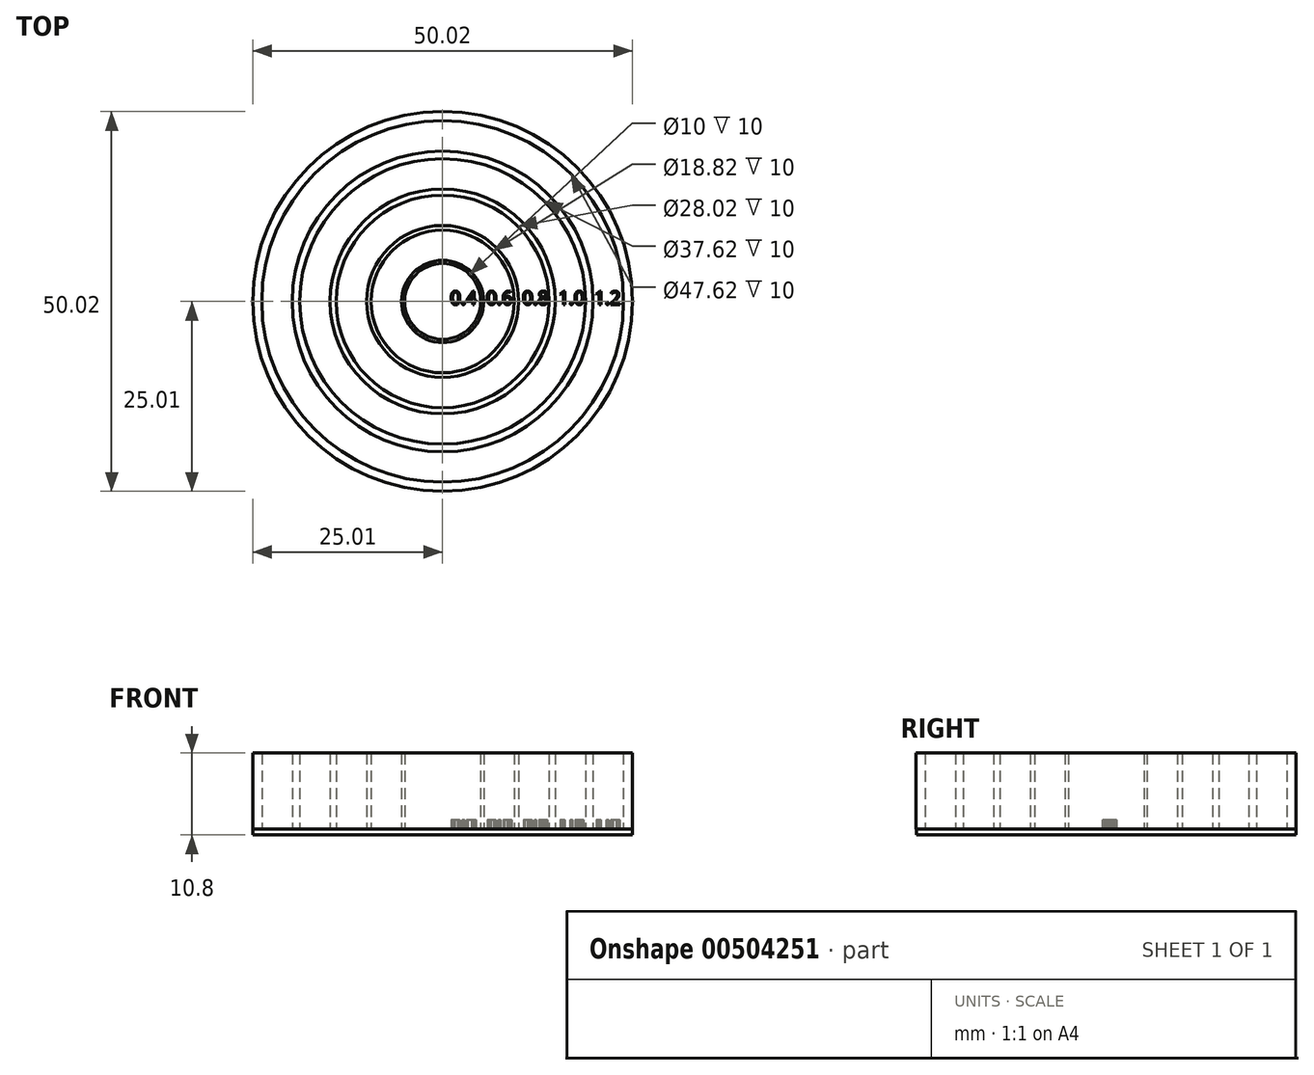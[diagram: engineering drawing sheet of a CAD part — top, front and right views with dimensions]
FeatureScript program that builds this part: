
annotation { "Feature Type Name" : "Feature", "Feature Type Description" : "" }
export const myFeature = defineFeature(function(context is Context, id is Id, definition is map)
    precondition{}
    {
        {
            var Q0;
            Q0=qCreatedBy(makeId("Top.planeOp"),FACE);
            var sketch = newSketch(context, id + "F0", { "sketchPlane" : qUnion([Q0])});
            skCircle(sketch, "E0", {"center": v(0, 0) * mm, "radius": 25 * mm});
            skSolve(sketch);
        }
        {
            var Q0;
            Q0=makeQuery(id+"F0.imprint","IMPRINT",FACE,{"disambiguationData":[TD([[makeQuery(id+"F0.imprint","IMPRINT",EDGE,{"derivedFrom":sQuery(id+"F0.wireOp",EDGE,"E0")}),1.0]])]});
            extrude(context, id + "F1", {"entities" : qUnion([Q0]), "depth" : 0.8 * mm});
        }
        {
            var Q0;
            Q0=makeQuery(id+"F1.opExtrude","CAP_FACE",FACE,{"disambiguationData":[OSD([sQuery(id+"F0.wireOp",EDGE,"E0")])],"isStart":false});
            var sketch = newSketch(context, id + "F2", { "sketchPlane" : qUnion([Q0])});
            skCircle(sketch, "E1", {"center": v(0, 0) * mm, "radius": 5 * mm});
            skCircle(sketch, "E2", {"center": v(0, 0) * mm, "radius": 5.4 * mm});
            skCircle(sketch, "E3", {"center": v(0, 0) * mm, "radius": 9.4 * mm});
            skCircle(sketch, "E4", {"center": v(0, 0) * mm, "radius": 10 * mm});
            skCircle(sketch, "E5", {"center": v(0, 0) * mm, "radius": 14 * mm});
            skCircle(sketch, "E6", {"center": v(0, 0) * mm, "radius": 14.8 * mm});
            skCircle(sketch, "E7", {"center": v(0, 0) * mm, "radius": 18.8 * mm});
            skCircle(sketch, "E8", {"center": v(0, 0) * mm, "radius": 19.81 * mm});
            skCircle(sketch, "E9", {"center": v(0, 0) * mm, "radius": 23.81 * mm});
            skCircle(sketch, "E10", {"center": v(0, 0) * mm, "radius": 25.01 * mm});
            skSolve(sketch);
        }
        {
            var Q0;
            Q0 = qSketchRegion(id + "F2", true);
            var Q1;
            Q1=makeQuery(id+"F2.imprint","IMPRINT",FACE,{"disambiguationData":[TD([[makeQuery(id+"F2.imprint","IMPRINT",EDGE,{"derivedFrom":sQuery(id+"F2.wireOp",EDGE,"E7")}),-1.0]])]});
            var Q2;
            Q2=makeQuery(id+"F2.imprint","IMPRINT",FACE,{"disambiguationData":[TD([[makeQuery(id+"F2.imprint","IMPRINT",EDGE,{"derivedFrom":sQuery(id+"F2.wireOp",EDGE,"E5")}),-1.0]])]});
            var Q3;
            Q3=makeQuery(id+"F2.imprint","IMPRINT",FACE,{"disambiguationData":[TD([[makeQuery(id+"F2.imprint","IMPRINT",EDGE,{"derivedFrom":sQuery(id+"F2.wireOp",EDGE,"E3")}),-1.0]])]});
            var Q4;
            Q4=makeQuery(id+"F2.imprint","IMPRINT",FACE,{"disambiguationData":[TD([[makeQuery(id+"F2.imprint","IMPRINT",EDGE,{"derivedFrom":sQuery(id+"F2.wireOp",EDGE,"E1")}),-1.0]])]});
            extrude(context, id + "F3", {"entities" : qUnion([Q0, Q1, Q2, Q3, Q4]), "operationType" : NewBodyOperationType.ADD, "depth" : 10 * mm});
        }
        {
            var Q0;
            Q0=qCreatedBy(makeId("Top.planeOp"),FACE);
            var sketch = newSketch(context, id + "F4", { "sketchPlane" : qUnion([Q0])});
            skText(sketch, "E11", { "text": "0.4  0.6  0.8  1.0  1.2", "fontName": "OpenSans-Regular.ttf"});
            const initialGuessF4  = {"E11": [0.001, -0.00041, 1, 0, 0.00177]};
            skSetInitialGuess(sketch, initialGuessF4);
            skSolve(sketch);
        }
        {
            var Q0;
            Q0 = qSketchRegion(id + "F4", true);
            extrude(context, id + "F5", {"entities" : qUnion([Q0]), "operationType" : NewBodyOperationType.ADD, "depth" : 2 * mm});
        }
    });
